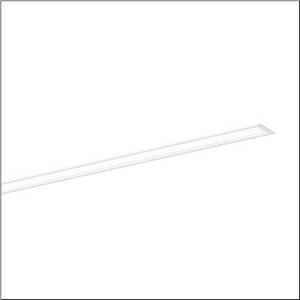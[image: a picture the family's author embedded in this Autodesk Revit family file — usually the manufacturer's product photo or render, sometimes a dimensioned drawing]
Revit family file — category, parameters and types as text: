
# Revit family: silica_r__21_51mx13tat4w_7811
name_source: partatom
category: Lighting Fixtures
units: mm (PartAtom-declared; Revit-internal decimal feet)

## family parameters
Cut with Voids When Loaded = No
Host = Face
Light Source = No
Part Type = Normal
Room Calculation Point = No
Round Connector Dimension = Use Diameter
Shared = No

## types (1)
- --- (1 x LED, 3230 lm, 32.4 W, 6500K)
    Apparent Load = 32 VA
    CIE Flux Codes = 78 96 99 100 100
    Color Rendering = 80
    Color Temperature = 6500K
    Default Elevation = 1800 mm
    Description = Silica® 21, office luminaire, primary optical cover: prismatic diffuser, of PMMA, CAT 2 (L<= 3000cd/m²), light emission: direct distribution, primary light characteristic: symmetric, installation type: recessed, LED, rated luminous flux: 3.230lm, luminous efficacy: 95lm/W, light colour: 8tw, colour temperature: 2700..6500K, with terminal, 3+2-pole, max. 2.5mm², mains connection: 220..240V, AC, 50/60Hz, rated input power: 34W, luminaire housing, of aluminium, traffic white (RAL 9016), length: 1.228mm, width: 79mm, height: 53mm, protection rating (complete): IP20, insulation class (complete): insulation class I (protective earthing), certification: CE, permissible operating ambient temperature: 0..+35°C, standard: EN 50419, packaging unit: 1 piece
    Height = 0 mm  [stored 0 ft]
    Lamp = 1 x LED
    Lamp Light Flux = 3230 lm
    Lamp Power = 32.4 W
    Lamp count = 1
    Length = 1227 mm
    Luminous efficacy = 100 lm/W
    Manufacturer = Siteco
    ModVariant = No
    Model = 51MX13TAT4W
    Mounting Place = Ceiling
    Mounting Type = Recessed
    Number of Poles = 1
    OnlyDefault = Yes
    Power Factor = 1
    Product Name = Silica® 21
    Product group = office luminaire | ceiling recessed
    ProductGroupID = 400
    Protection Class = Protection class I
    Protection Degree = IP 20
    RLX_Detail_Level = 1
    RlxData = <blob elided: 13041 chars, md5=36300b5c>
    Socket = socket
    Standby Power = 0 W
    System Light Flux = 3230 lm
    System Power = 32 W
    Type Comments = individual setting
    Type Image = l_1251708.jpg
    URL = http://relux.com
    VarID = @adj_045945
    Voltage = 0 V
    Weight = 0.00 kg
    Width = 79 mm

note: [stored X ft] marks values corroborated as IEEE doubles in the binary element streams (Revit-internal decimal feet)

## geometry (parser evidence)
native form markers: Sweep x9
no freeform markers — native parametric forms only
